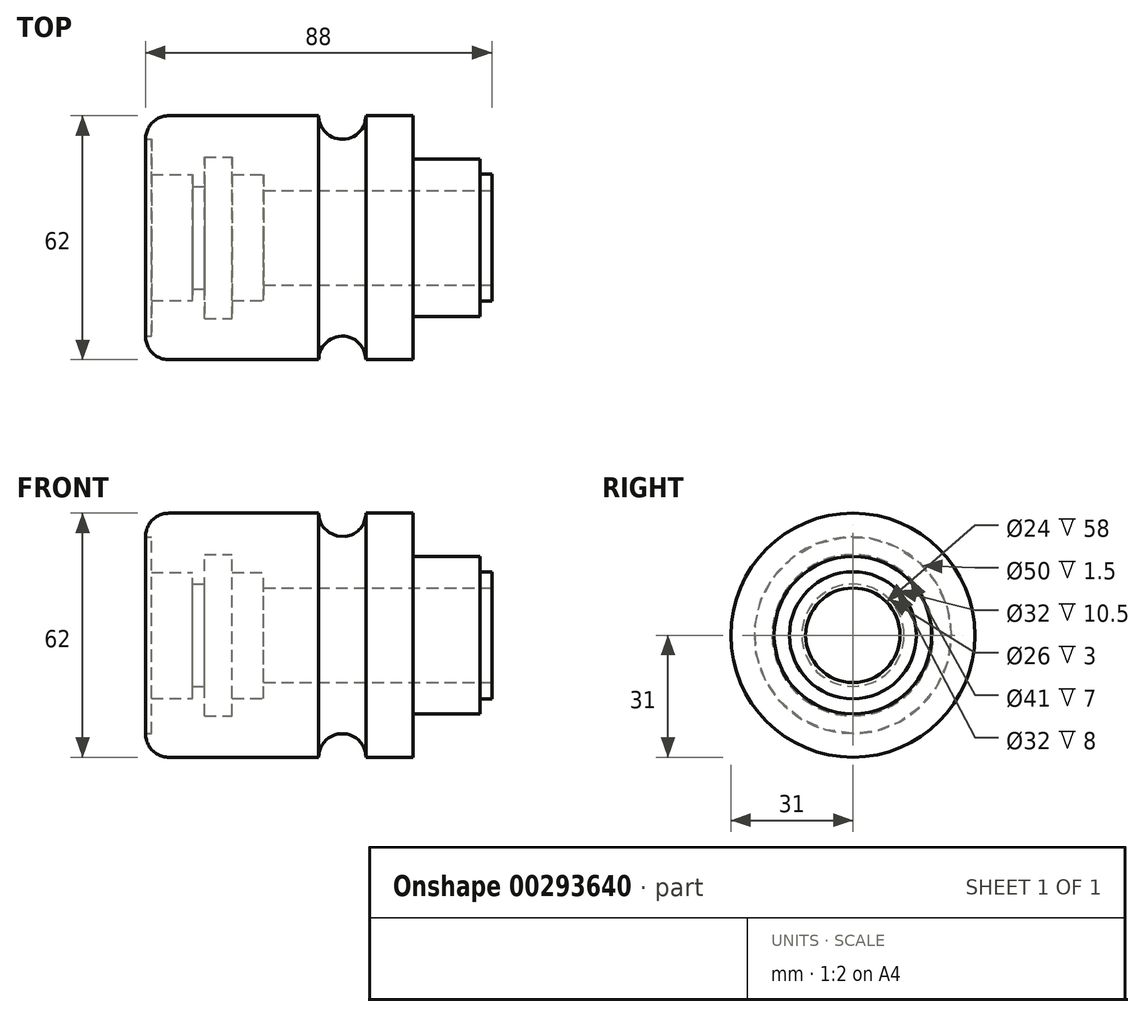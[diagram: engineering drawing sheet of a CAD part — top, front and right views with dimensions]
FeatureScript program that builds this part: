
annotation { "Feature Type Name" : "Feature", "Feature Type Description" : "" }
export const myFeature = defineFeature(function(context is Context, id is Id, definition is map)
    precondition{}
    {
        {
            var Q0;
            Q0=qCreatedBy(makeId("Front.planeOp"),FACE);
            var sketch = newSketch(context, id + "F0", { "sketchPlane" : qUnion([Q0])});
            skLineSegment(sketch, "E0", {"start": v(0, 0) * mm, "end": v(0, 25) * mm});
            skLineSegment(sketch, "E1", {"start": v(6, 31) * mm, "end": v(44, 31) * mm});
            skArc(sketch, "E2", {"start": v(44, 31) * mm, "mid": v(50, 25) * mm, "end": v(56, 31) * mm});
            skLineSegment(sketch, "E3", {"start": v(56, 31) * mm, "end": v(68, 31) * mm});
            skLineSegment(sketch, "E4", {"start": v(68, 31) * mm, "end": v(68, 20) * mm});
            skLineSegment(sketch, "E5", {"start": v(68, 20) * mm, "end": v(85, 20) * mm});
            skLineSegment(sketch, "E6", {"start": v(85, 20) * mm, "end": v(85, 16.12) * mm});
            skLineSegment(sketch, "E7", {"start": v(85, 16.12) * mm, "end": v(88, 16.12) * mm});
            skLineSegment(sketch, "E8", {"start": v(88, 16.12) * mm, "end": v(88, 0) * mm});
            skLineSegment(sketch, "E9", {"start": v(88, 0) * mm, "end": v(0, 0) * mm});
            skLineSegment(sketch, "E10", {"start": v(1.5, 16) * mm, "end": v(12, 16) * mm});
            skLineSegment(sketch, "E11", {"start": v(12, 16) * mm, "end": v(12, 13) * mm});
            skLineSegment(sketch, "E12", {"start": v(12, 0) * mm, "end": v(13.16, 0) * mm});
            skLineSegment(sketch, "E13", {"start": v(15, 13) * mm, "end": v(12, 13) * mm});
            skLineSegment(sketch, "E14", {"start": v(1.5, 0) * mm, "end": v(12, 0) * mm});
            skLineSegment(sketch, "E15", {"start": v(15, 13) * mm, "end": v(15, 20.5) * mm});
            skLineSegment(sketch, "E16", {"start": v(15, 20.5) * mm, "end": v(22, 20.5) * mm});
            skLineSegment(sketch, "E17", {"start": v(22, 20.5) * mm, "end": v(22, 16) * mm});
            skLineSegment(sketch, "E18", {"start": v(22, 16) * mm, "end": v(30, 16) * mm});
            skLineSegment(sketch, "E19", {"start": v(1.5, 0) * mm, "end": v(1.5, 25) * mm});
            skLineSegment(sketch, "E20", {"start": v(1.5, 25) * mm, "end": v(0, 25) * mm});
            skLineSegment(sketch, "E21", {"start": v(30, 16) * mm, "end": v(30, 12) * mm});
            skLineSegment(sketch, "E22", {"start": v(30, 12) * mm, "end": v(88, 12) * mm});
            skPoint(sketch, "E23.visualSharp", {"position": v(0, 31) * mm});
            skArc(sketch, "E23.filletArc", {"start": v(6, 31) * mm, "mid": v(1.76, 29.24) * mm, "end": v(0, 25) * mm});
            skSolve(sketch);
        }
        {
            var Q0;
            Q0=makeQuery(id+"F0.imprint","IMPRINT",FACE,{"disambiguationData":[TD([[makeQuery(id+"F0.imprint","IMPRINT",EDGE,{"derivedFrom":sQuery(id+"F0.wireOp",EDGE,"E1")}),-1.0]])]});
            var Q1;
            Q1=sQuery(id+"F0.wireOp",EDGE,"E9");
            revolve(context, id + "F1", {"entities" : qUnion([Q0]), "axis" : qUnion([Q1]), "revolveType" : RevolveType.FULL});
        }
    });
